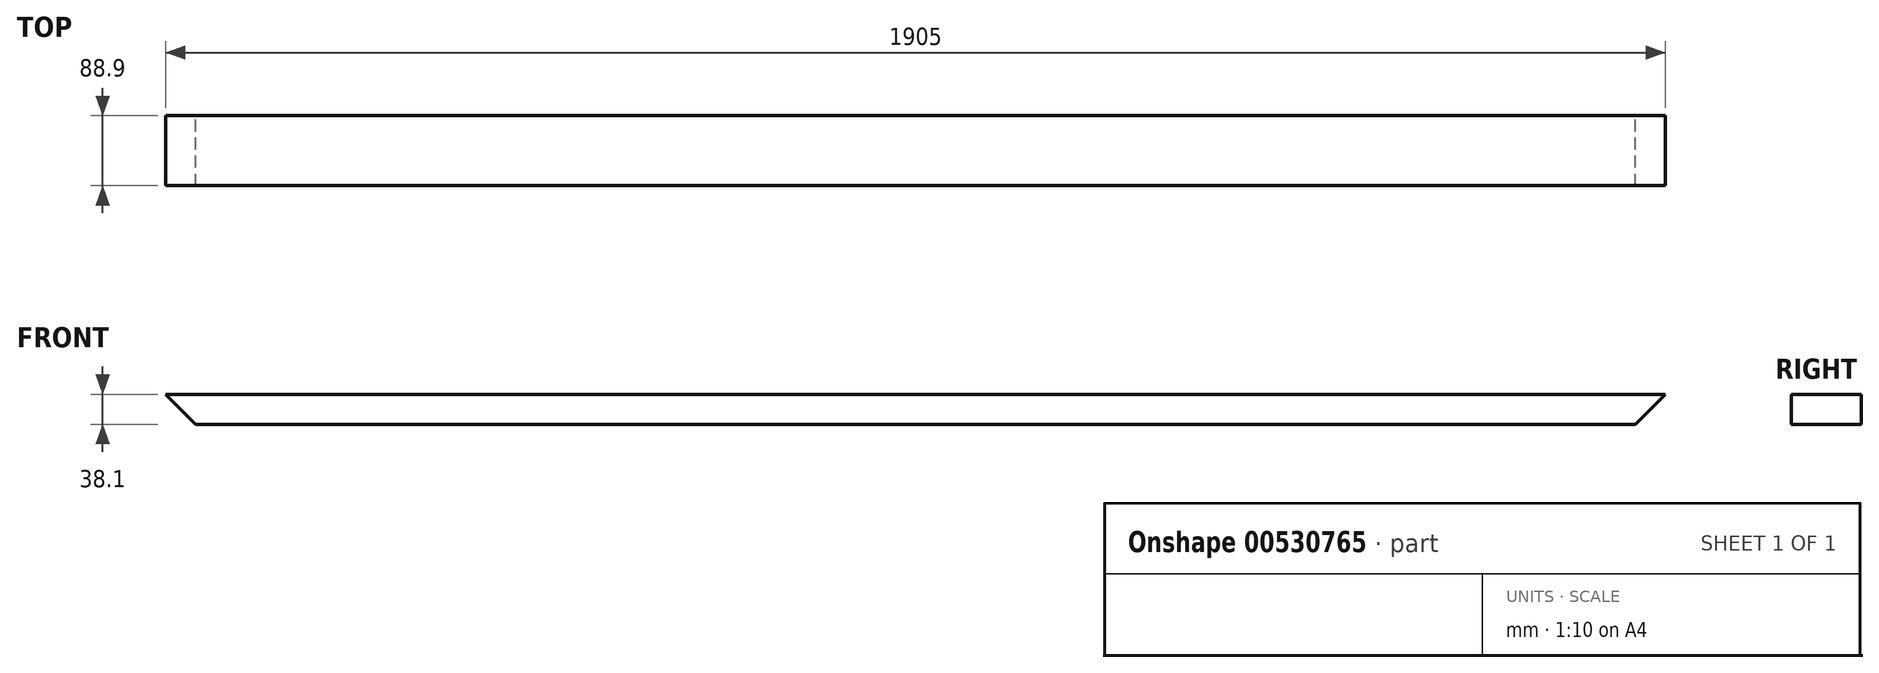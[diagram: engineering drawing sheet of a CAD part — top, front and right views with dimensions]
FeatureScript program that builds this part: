
annotation { "Feature Type Name" : "Feature", "Feature Type Description" : "" }
export const myFeature = defineFeature(function(context is Context, id is Id, definition is map)
    precondition{}
    {
        {
            var Q0;
            Q0=qCreatedBy(makeId("Front.planeOp"),FACE);
            var sketch = newSketch(context, id + "F0", { "sketchPlane" : qUnion([Q0])});
            skLineSegment(sketch, "E0", {"start": v(644.57, 0) * mm, "end": v(-1260.43, 0) * mm});
            skLineSegment(sketch, "E1", {"start": v(-1222.33, -38.1) * mm, "end": v(606.47, -38.1) * mm});
            skLineSegment(sketch, "E2", {"start": v(606.47, -38.1) * mm, "end": v(644.57, 0) * mm});
            skLineSegment(sketch, "E3", {"start": v(-1222.33, -38.1) * mm, "end": v(-1260.43, 0) * mm});
            skSolve(sketch);
        }
        {
            var Q0;
            Q0 = qSketchRegion(id + "F0", true);
            extrude(context, id + "F1", {"entities" : qUnion([Q0]), "depth" : 88.9 * mm, "offsetDistance" : 25.4 * mm});
        }
    });
